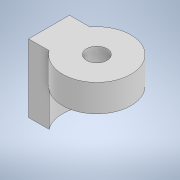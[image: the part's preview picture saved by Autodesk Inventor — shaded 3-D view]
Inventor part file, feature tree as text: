
AUTODESK INVENTOR PART (.ipt)
format: ipt  version: 2020 (Build 240168000, 168)  size: 138,240 bytes
history: native  units: in
note: dims shown in document units (in); Inventor stores cm internally (conversion verified against a paired STEP export)
features: extrude x4, sketch x4
ambient origin geometry x8: Origin, YZ Plane, XZ Plane, XY Plane, X Axis, Y Axis, Z Axis, Center Point
bodies: Solid1 (feature_tree)
feature tree (8):
  extrude  "Extrusion1"  Depth=1.9685in
  extrude  "Extrusion2"  Depth=0.5906in
  extrude  "Extrusion3"  Depth=1.378in
  extrude  "Extrusion4"  Depth=1.9685in TaperAngle=0.0deg
  sketch  "Sketch1"  dims[d0=1.9685in d1=1.9685in]
  sketch  "Sketch2"  dims[d2=0.7874in d3=0.0in d4=0.5906in]
  sketch  "Sketch3"  dims[d5=0.5906in d6=1.378in]
  sketch  "Sketch4"  dims[d7=1.9685in d8=1.9685in d9=0.0in d10=0.5906in d11=0.9843in d12=1.1811in d13=0.0in d14=1.1811in d15=0.5906in d16=0.5906in d17=0.4724in d18=1.1811in d19=0.0in]
